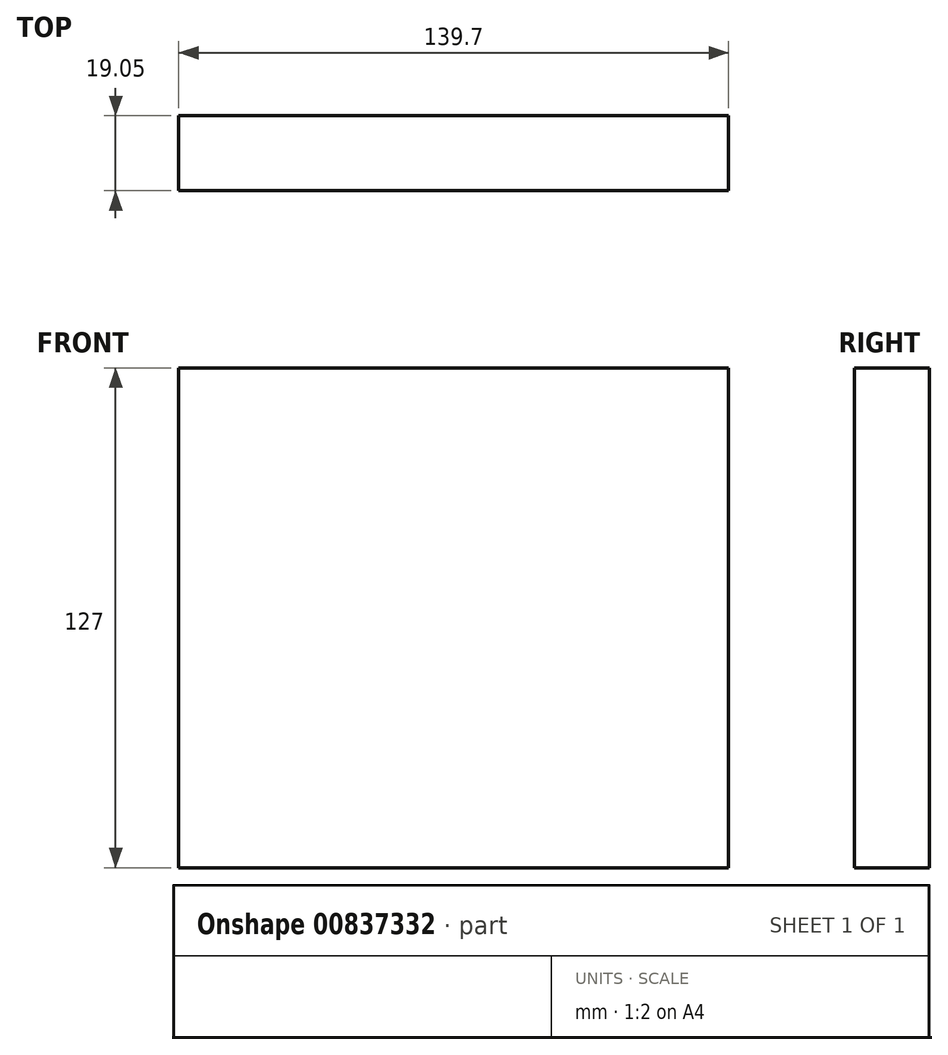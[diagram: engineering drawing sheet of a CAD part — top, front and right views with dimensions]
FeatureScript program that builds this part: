
annotation { "Feature Type Name" : "Feature", "Feature Type Description" : "" }
export const myFeature = defineFeature(function(context is Context, id is Id, definition is map)
    precondition{}
    {
        {
            var Q0;
            Q0=qCreatedBy(makeId("Front.planeOp"),FACE);
            var sketch = newSketch(context, id + "F0", { "sketchPlane" : qUnion([Q0])});
            skLineSegment(sketch, "E0.bottom", {"start": v(0, 0) * mm, "end": v(139.7, 0) * mm});
            skLineSegment(sketch, "E0.top", {"start": v(0, 127) * mm, "end": v(139.7, 127) * mm});
            skLineSegment(sketch, "E0.left", {"start": v(0, 0) * mm, "end": v(0, 127) * mm});
            skLineSegment(sketch, "E0.right", {"start": v(139.7, 0) * mm, "end": v(139.7, 127) * mm});
            skSolve(sketch);
        }
        {
            var Q0;
            Q0=makeQuery(id+"F0.imprint","IMPRINT",FACE,{"disambiguationData":[TD([[makeQuery(id+"F0.imprint","IMPRINT",EDGE,{"derivedFrom":sQuery(id+"F0.wireOp",EDGE,"E0.bottom")}),1.0]])]});
            extrude(context, id + "F1", {"entities" : qUnion([Q0]), "depth" : 19.05 * mm, "offsetDistance" : 25.4 * mm});
        }
    });
